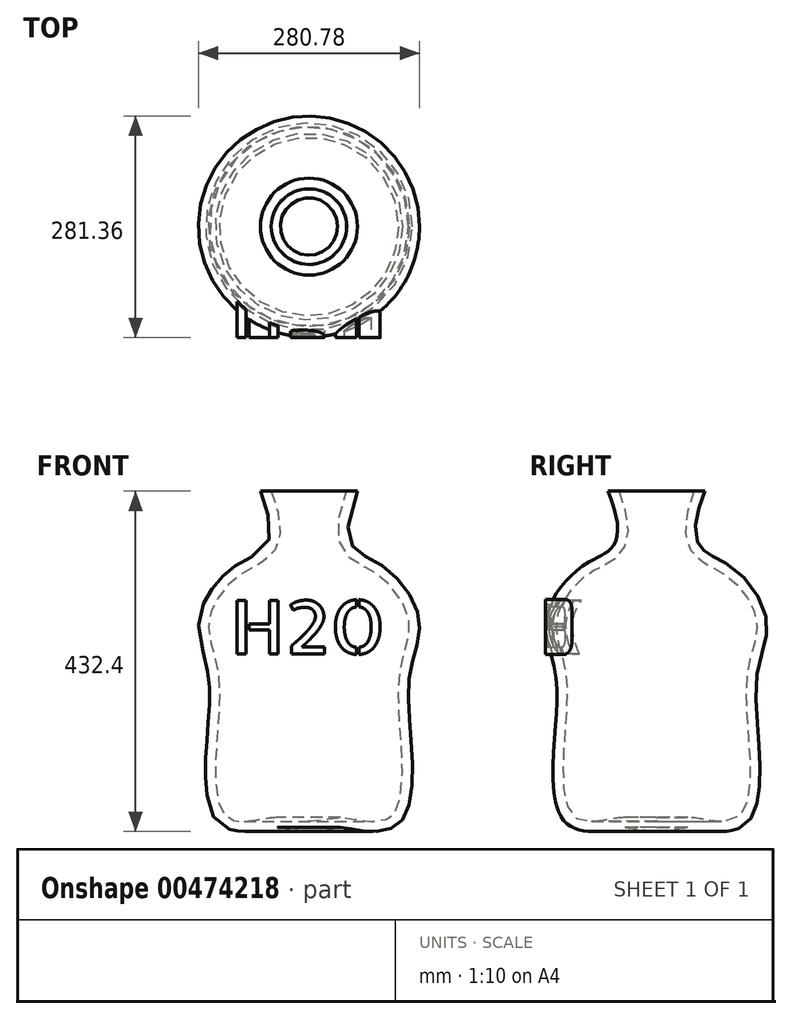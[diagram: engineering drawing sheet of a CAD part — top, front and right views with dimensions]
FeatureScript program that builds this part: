
annotation { "Feature Type Name" : "Feature", "Feature Type Description" : "" }
export const myFeature = defineFeature(function(context is Context, id is Id, definition is map)
    precondition{}
    {
        {
            var Q0;
            Q0=qCreatedBy(makeId("Front.planeOp"),FACE);
            var sketch = newSketch(context, id + "F0", { "sketchPlane" : qUnion([Q0])});
            skFitSpline(sketch, "E0", {"points": [v(0, 0) * mm, v(39.38, 4.3) * mm, v(70.76, 0) * mm, v(115.8, 11.05) * mm, v(130.83, 98.64) * mm, v(128.32, 201.24) * mm, v(139.7, 269.52) * mm, v(88.28, 340.14) * mm, v(61.6, 431.8) * mm], "startDerivative": vector(502.56, 0) * mm, "endDerivative": vector(600.08, 1517.85) * mm});
            skLineSegment(sketch, "E1", {"start": v(0, 0) * mm, "end": v(0, 431.8) * mm});
            skLineSegment(sketch, "E2", {"start": v(61.6, 431.8) * mm, "end": v(0, 431.8) * mm});
            skFitSpline(sketch, "E3.0", {"points": [v(0, 12.7) * mm, v(2.26, 12.7) * mm, v(6.63, 12.9) * mm, v(12.9, 13.59) * mm, v(19.06, 14.55) * mm, v(24.2, 15.42) * mm, v(28.4, 16.07) * mm, v(31.62, 16.5) * mm, v(34.37, 16.77) * mm, v(36.62, 16.91) * mm, v(38.33, 16.98) * mm, v(40.07, 17) * mm, v(41.78, 16.98) * mm, v(43.46, 16.9) * mm, v(45.66, 16.76) * mm, v(48.33, 16.49) * mm, v(51.41, 16.06) * mm, v(54.4, 15.57) * mm, v(58.28, 14.87) * mm, v(62.04, 14.15) * mm, v(65.78, 13.5) * mm, v(68.61, 13.06) * mm, v(71.01, 12.75) * mm, v(72.97, 12.53) * mm, v(74.96, 12.35) * mm, v(77.5, 12.18) * mm, v(81.63, 12.06) * mm, v(86.8, 12.21) * mm, v(92.72, 13) * mm, v(97.15, 14.2) * mm, v(100.28, 15.46) * mm, v(102.4, 16.55) * mm, v(104.3, 17.78) * mm, v(105.57, 18.81) * mm, v(106.36, 19.56) * mm, v(106.74, 19.94) * mm, v(107.12, 20.34) * mm, v(107.62, 20.9) * mm, v(108.24, 21.66) * mm, v(109.22, 23) * mm, v(110.42, 24.93) * mm, v(111.78, 27.64) * mm, v(113.06, 30.73) * mm, v(114.6, 35.33) * mm, v(116.21, 41.92) * mm, v(117.6, 50.92) * mm, v(118.44, 60.77) * mm, v(118.82, 71.26) * mm, v(118.78, 82.16) * mm, v(118.47, 91.43) * mm, v(118.1, 98.87) * mm, v(117.67, 106.3) * mm, v(117.02, 115.54) * mm, v(116.16, 126.56) * mm, v(115.3, 137.5) * mm, v(114.53, 148.33) * mm, v(113.94, 159.05) * mm, v(113.62, 169.63) * mm, v(113.65, 180.07) * mm, v(114.08, 188.64) * mm, v(114.7, 195.42) * mm, v(115.22, 199.61) * mm, v(115.73, 202.95) * mm, v(116.3, 206.26) * mm, v(117.09, 210.3) * mm, v(118.15, 214.98) * mm, v(119.28, 219.52) * mm, v(120.45, 223.91) * mm, v(122.02, 229.6) * mm, v(123.9, 236.38) * mm, v(125.8, 244.07) * mm, v(127.14, 251.35) * mm, v(127.68, 257.13) * mm, v(127.7, 261.65) * mm, v(127.54, 264.46) * mm, v(127.28, 266.7) * mm, v(126.95, 268.95) * mm, v(126.35, 271.86) * mm, v(125.36, 275.46) * mm, v(124.1, 279.16) * mm, v(122.58, 282.93) * mm, v(120.22, 288) * mm, v(116.67, 294.37) * mm, v(111.55, 301.9) * mm, v(105.7, 309.1) * mm, v(100.35, 314.7) * mm, v(95.85, 318.85) * mm, v(92.38, 321.8) * mm, v(89.43, 324.08) * mm, v(87.05, 325.8) * mm, v(85.25, 327.03) * mm, v(83.75, 328.01) * mm, v(82.54, 328.77) * mm, v(81.64, 329.32) * mm, v(80.72, 329.86) * mm, v(79.49, 330.57) * mm, v(77.9, 331.45) * mm, v(75.96, 332.49) * mm, v(73.3, 333.87) * mm, v(69.87, 335.61) * mm, v(65.62, 337.8) * mm, v(61.3, 340.2) * mm, v(56.93, 342.92) * mm, v(52.6, 346.12) * mm, v(48.43, 349.93) * mm, v(44.6, 354.47) * mm, v(41.33, 359.79) * mm, v(38.83, 365.8) * mm, v(37.2, 372.38) * mm, v(36.46, 379.46) * mm, v(36.56, 387.07) * mm, v(37.49, 395.27) * mm, v(39.22, 404.17) * mm, v(42.66, 417.14) * mm, v(46.55, 428.28) * mm, v(49.79, 436.47) * mm]});
            skSolve(sketch);
        }
        {
            var Q0;
            {var subQ0=sQuery(id+"F0.wireOp",EDGE,"E0");Q0=makeQuery(id+"F0.imprint","IMPRINT",FACE,{"disambiguationData":[TD([[makeQuery(id+"F0.imprint","IMPRINT",EDGE,{"derivedFrom":subQ0}),1.0]])]});}
            var Q1;
            Q1=sQuery(id+"F0.wireOp",EDGE,"E1");
            revolve(context, id + "F1", {"entities" : qUnion([Q0]), "axis" : qUnion([Q1]), "revolveType" : RevolveType.FULL});
        }
        {
            var Q0;
            Q0=qCreatedBy(makeId("Front.planeOp"),FACE);
            cPlane(context, id + "F2", {"entities" : qUnion([Q0]), "cplaneType" : CPlaneType.OFFSET, "offset" : 140.97 * mm, "width" : 152.4 * mm, "height" : 152.4 * mm});
        }
        {
            var Q0;
            Q0=qCreatedBy(id+"F2.planeOp",FACE);
            var sketch = newSketch(context, id + "F3", { "sketchPlane" : qUnion([Q0])});
            skText(sketch, "E4", { "text": "H2O", "fontName": "AllertaStencil-Regular.ttf"});
            const initialGuessF3  = {"E4": [-0.09978, 0.22462, 1, 0, 0.06823]};
            skSetInitialGuess(sketch, initialGuessF3);
            skSolve(sketch);
        }
        {
            var Q0;
            Q0 = qSketchRegion(id + "F3", true);
            var Q1;
            Q1=makeQuery(id+"F1.opRevolve","SWEPT_FACE",FACE,{"disambiguationData":[OSD([sQuery(id+"F0.wireOp",EDGE,"E3.0")])]});
            extrude(context, id + "F4", {"entities" : qUnion([Q0]), "operationType" : NewBodyOperationType.ADD, "endBound" : BoundingType.UP_TO_SURFACE, "oppositeDirection" : true, "endBoundEntityFace" : qUnion([Q1]), "depth" : 25.4 * mm});
        }
    });
